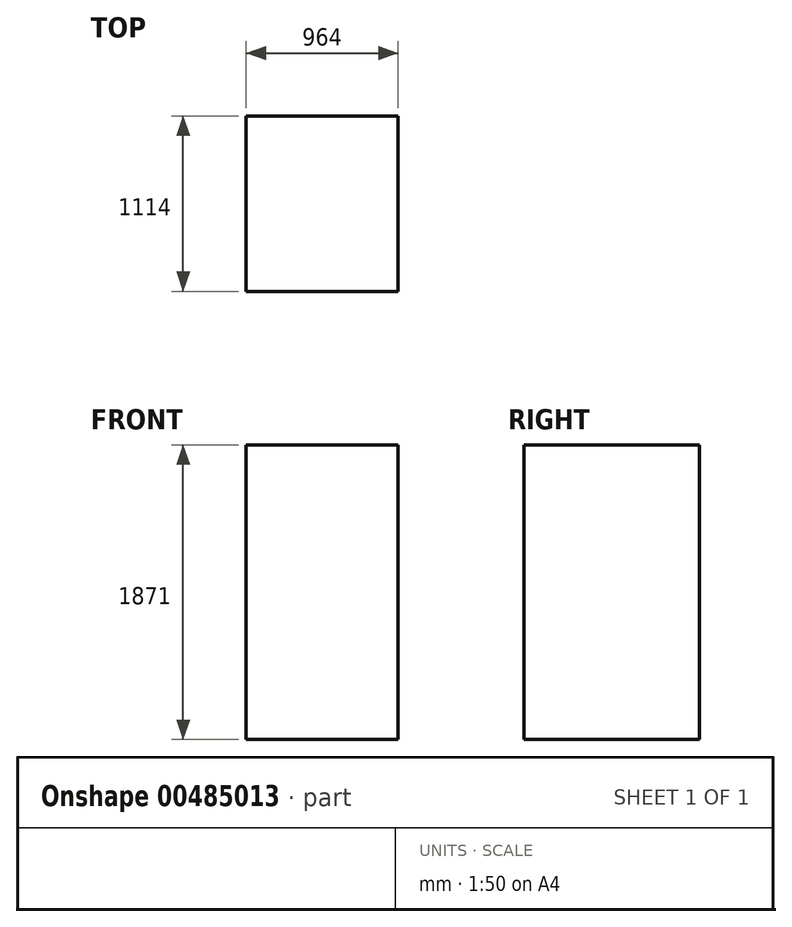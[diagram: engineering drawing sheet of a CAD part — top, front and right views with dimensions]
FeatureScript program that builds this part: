
annotation { "Feature Type Name" : "Feature", "Feature Type Description" : "" }
export const myFeature = defineFeature(function(context is Context, id is Id, definition is map)
    precondition{}
    {
        {
            var Q0;
            Q0=qCreatedBy(makeId("Top.planeOp"),FACE);
            var sketch = newSketch(context, id + "F0", { "sketchPlane" : qUnion([Q0])});
            skLineSegment(sketch, "E0.bottom", {"start": v(482, 557) * mm, "end": v(-482, 557) * mm});
            skLineSegment(sketch, "E0.top", {"start": v(482, -557) * mm, "end": v(-482, -557) * mm});
            skLineSegment(sketch, "E0.left", {"start": v(482, 557) * mm, "end": v(482, -557) * mm});
            skLineSegment(sketch, "E0.right", {"start": v(-482, 557) * mm, "end": v(-482, -557) * mm});
            skPoint(sketch, "E0.middle", {"position": v(0, 0) * mm});
            skSolve(sketch);
        }
        {
            var Q0;
            Q0 = qSketchRegion(id + "F0", true);
            extrude(context, id + "F1", {"entities" : qUnion([Q0]), "depth" : 1871 * mm});
        }
    });
